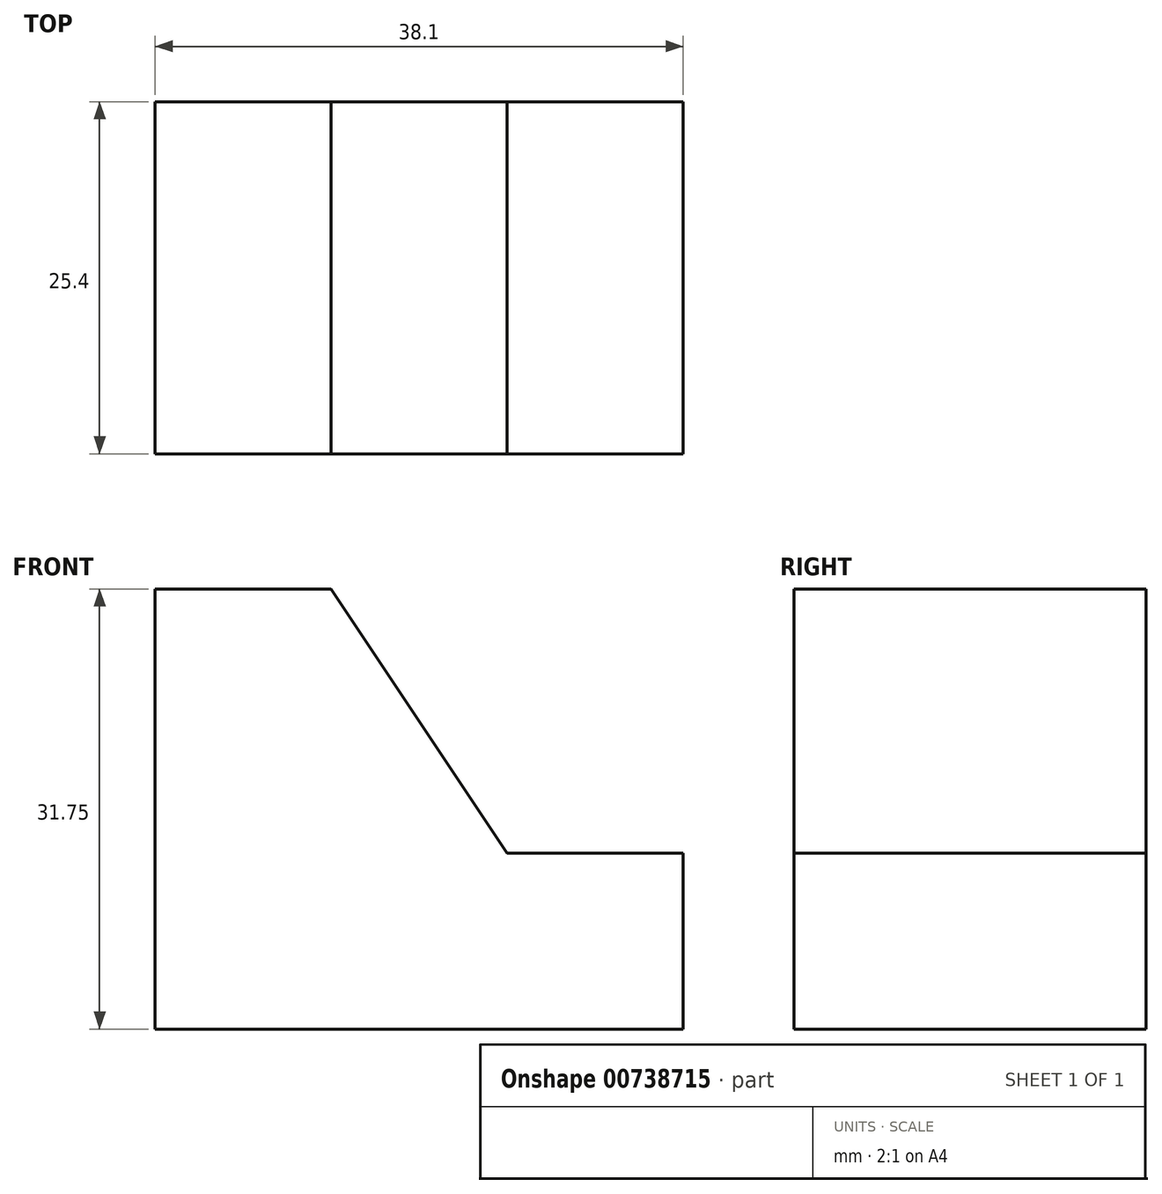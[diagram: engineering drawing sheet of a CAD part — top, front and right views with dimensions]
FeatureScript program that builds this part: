
annotation { "Feature Type Name" : "Feature", "Feature Type Description" : "" }
export const myFeature = defineFeature(function(context is Context, id is Id, definition is map)
    precondition{}
    {
        {
            var Q0;
            Q0=qCreatedBy(makeId("Front.planeOp"),FACE);
            var sketch = newSketch(context, id + "F0", { "sketchPlane" : qUnion([Q0])});
            skLineSegment(sketch, "E0", {"start": v(0, 31.75) * mm, "end": v(12.7, 31.75) * mm});
            skLineSegment(sketch, "E1", {"start": v(12.7, 31.75) * mm, "end": v(25.4, 12.7) * mm});
            skLineSegment(sketch, "E2", {"start": v(25.4, 12.7) * mm, "end": v(38.1, 12.7) * mm});
            skLineSegment(sketch, "E3", {"start": v(38.1, 12.7) * mm, "end": v(38.1, 0) * mm});
            skLineSegment(sketch, "E4", {"start": v(38.1, 0) * mm, "end": v(0, 0) * mm});
            skLineSegment(sketch, "E5", {"start": v(0, 0) * mm, "end": v(0, 31.75) * mm});
            skSolve(sketch);
        }
        {
            var Q0;
            Q0 = qSketchRegion(id + "F0", true);
            extrude(context, id + "F1", {"entities" : qUnion([Q0]), "depth" : 25.4 * mm, "offsetDistance" : 25.4 * mm});
        }
    });
